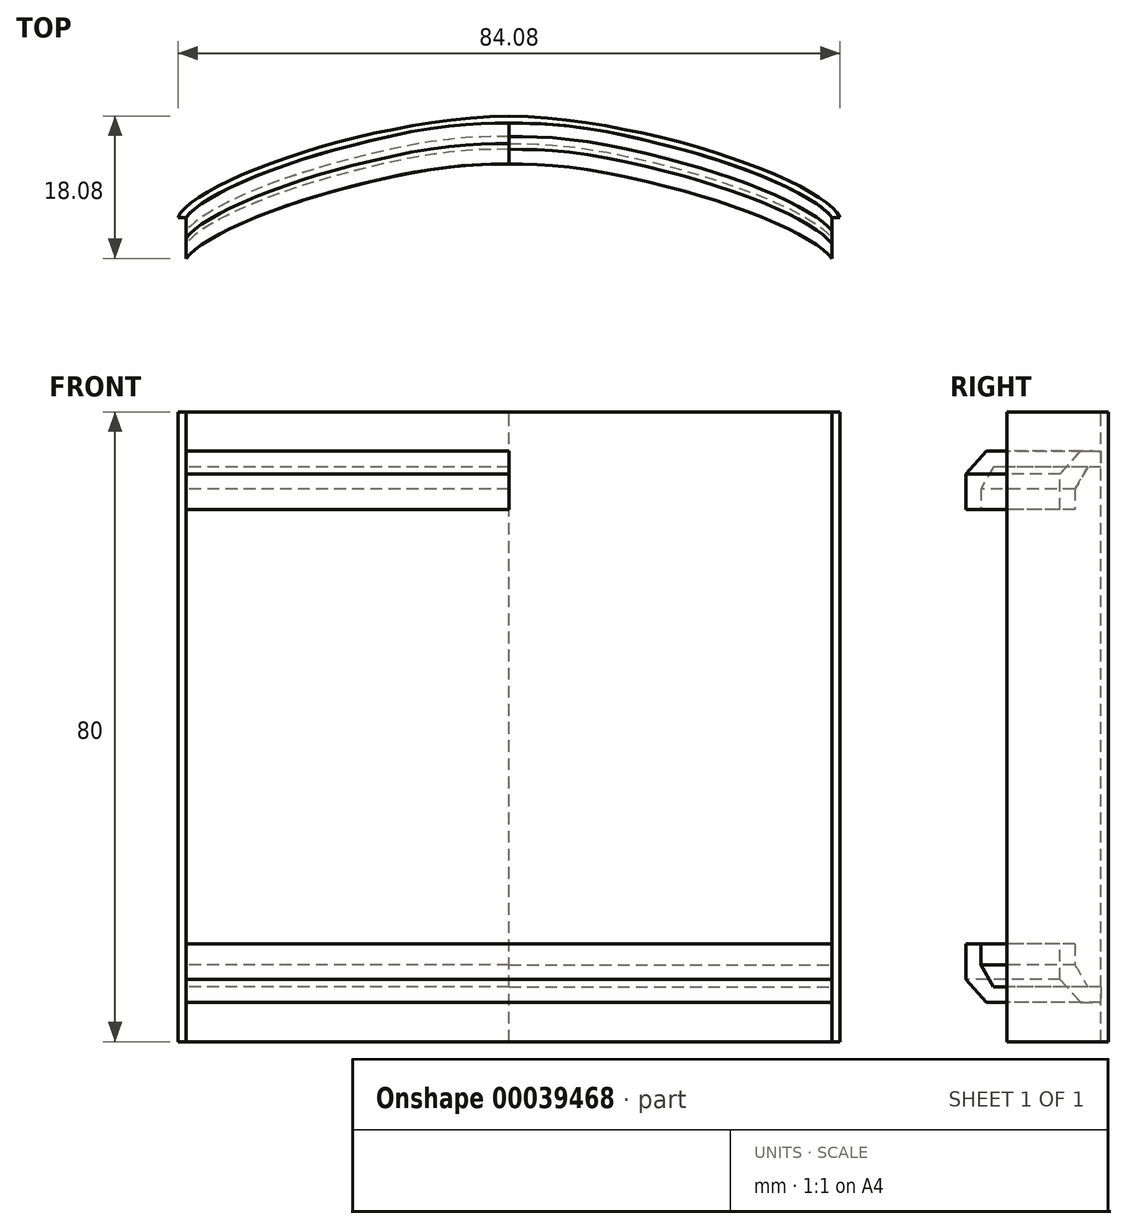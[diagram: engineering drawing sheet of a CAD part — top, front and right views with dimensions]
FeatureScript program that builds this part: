
annotation { "Feature Type Name" : "Feature", "Feature Type Description" : "" }
export const myFeature = defineFeature(function(context is Context, id is Id, definition is map)
    precondition{}
    {
        {
            var Q0;
            Q0=qCreatedBy(makeId("Top.planeOp"),FACE);
            var sketch = newSketch(context, id + "F0", { "sketchPlane" : qUnion([Q0])});
            skFitSpline(sketch, "E0", {"points": [v(-42.04, 0) * mm, v(0, 12.87) * mm], "startDerivative": vector(5.48, 12.98) * mm, "endDerivative": vector(55.38, 1.16) * mm});
            skFitSpline(sketch, "E1.MirrorCS", {"points": [v(42.04, 0) * mm, v(0, 12.87) * mm], "startDerivative": vector(-5.48, 12.98) * mm, "endDerivative": vector(-55.38, 1.16) * mm});
            skFitSpline(sketch, "E2.0", {"points": [v(41.2, -0.35) * mm, v(41.18, -0.28) * mm, v(41.08, -0.1) * mm, v(40.72, 0.36) * mm, v(39.98, 1.06) * mm, v(38.64, 1.99) * mm, v(36.35, 3.31) * mm, v(32.63, 5.04) * mm, v(27.1, 7.09) * mm, v(20.79, 8.95) * mm, v(11.7, 11) * mm, v(4.53, 11.87) * mm, v(-0.02, 11.97) * mm]});
            skFitSpline(sketch, "E2.1", {"points": [v(-41.2, -0.35) * mm, v(-41.18, -0.28) * mm, v(-41.08, -0.1) * mm, v(-40.72, 0.36) * mm, v(-39.98, 1.06) * mm, v(-38.64, 1.99) * mm, v(-36.35, 3.31) * mm, v(-32.63, 5.04) * mm, v(-27.1, 7.09) * mm, v(-20.79, 8.95) * mm, v(-11.7, 11) * mm, v(-4.53, 11.87) * mm, v(0.02, 11.97) * mm]});
            skLineSegment(sketch, "E3", {"start": v(-42.04, 0) * mm, "end": v(-41, 0) * mm});
            skLineSegment(sketch, "E4", {"start": v(41, 0) * mm, "end": v(42.04, 0) * mm});
            skSolve(sketch);
        }
        {
            var Q0;
            Q0=makeQuery(id+"F0.imprint","IMPRINT",FACE,{"disambiguationData":[TD([[makeQuery(id+"F0.imprint","IMPRINT",EDGE,{"derivedFrom":sQuery(id+"F0.wireOp",EDGE,"E0")}),-1.0]])]});
            extrude(context, id + "F1", {"entities" : qUnion([Q0]), "endBound" : BoundingType.SYMMETRIC, "oppositeDirection" : true, "depth" : 80 * mm});
        }
        {
            var Q0;
            Q0=qCreatedBy(makeId("Right.planeOp"),FACE);
            var sketch = newSketch(context, id + "F2", { "sketchPlane" : qUnion([Q0])});
            skLineSegment(sketch, "E5", {"start": v(11.97, 0) * mm, "end": v(11.97, -37.82) * mm, "construction": true});
            skLineSegment(sketch, "E6", {"start": v(11.97, -34.98) * mm, "end": v(11.97, -33.02) * mm});
            skLineSegment(sketch, "E7", {"start": v(11.97, -33.02) * mm, "end": v(10.28, -33.02) * mm});
            skLineSegment(sketch, "E8", {"start": v(10.28, -33.02) * mm, "end": v(8.65, -30.23) * mm});
            skLineSegment(sketch, "E9", {"start": v(8.65, -30.23) * mm, "end": v(8.65, -27.59) * mm});
            skLineSegment(sketch, "E10", {"start": v(8.65, -27.59) * mm, "end": v(6.76, -27.59) * mm});
            skLineSegment(sketch, "E11", {"start": v(6.76, -27.59) * mm, "end": v(6.76, -32.11) * mm});
            skLineSegment(sketch, "E12", {"start": v(6.76, -32.11) * mm, "end": v(9.37, -35.03) * mm});
            skLineSegment(sketch, "E13", {"start": v(9.37, -35.03) * mm, "end": v(11.97, -34.98) * mm});
            skSolve(sketch);
        }
        {
            var Q0;
            Q0=makeQuery(id+"F2.imprint","IMPRINT",FACE,{"disambiguationData":[TD([[makeQuery(id+"F2.imprint","IMPRINT",EDGE,{"derivedFrom":sQuery(id+"F2.wireOp",EDGE,"E6")}),1.0]])]});
            var Q1;
            Q1=makeQuery(id+"F1.opExtrude","CAP_EDGE",EDGE,{"disambiguationData":[OSD([sQuery(id+"F0.wireOp",EDGE,"E2.1")])],"isStart":false});
            sweep(context, id + "F3", {"profiles" : qUnion([Q0]), "path" : qUnion([Q1]), "keepProfileOrientation" : true});
        }
        {
            var Q0;
            Q0=makeQuery(id+"F3.opSweep","CAP_FACE",FACE,{"disambiguationData":[OSD([sQuery(id+"F0.wireOp",EDGE,"E2.0"),sQuery(id+"F0.wireOp",EDGE,"E2.1"),sQuery(id+"F2.wireOp",EDGE,"E6"),sQuery(id+"F2.wireOp",EDGE,"E7"),sQuery(id+"F2.wireOp",EDGE,"E8"),sQuery(id+"F2.wireOp",EDGE,"E9"),sQuery(id+"F2.wireOp",EDGE,"E10"),sQuery(id+"F2.wireOp",EDGE,"E11"),sQuery(id+"F2.wireOp",EDGE,"E12"),sQuery(id+"F2.wireOp",EDGE,"E13")])],"isStart":true});
            var Q1;
            Q1=makeQuery(id+"F1.opExtrude","CAP_EDGE",EDGE,{"disambiguationData":[OSD([sQuery(id+"F0.wireOp",EDGE,"E2.0")])],"isStart":false});
            sweep(context, id + "F4", {"profiles" : qUnion([Q0]), "path" : qUnion([Q1]), "keepProfileOrientation" : true});
        }
        {
            var Q0;
            Q0=makeQuery(id+"F3.opSweep","SWEPT_BODY",BODY,{"disambiguationData":[OSD([sQuery(id+"F0.wireOp",EDGE,"E2.1"),sQuery(id+"F2.wireOp",EDGE,"E6"),sQuery(id+"F2.wireOp",EDGE,"E7"),sQuery(id+"F2.wireOp",EDGE,"E8"),sQuery(id+"F2.wireOp",EDGE,"E9"),sQuery(id+"F2.wireOp",EDGE,"E10"),sQuery(id+"F2.wireOp",EDGE,"E11"),sQuery(id+"F2.wireOp",EDGE,"E12"),sQuery(id+"F2.wireOp",EDGE,"E13")])]});
            var Q1;
            Q1=qCreatedBy(makeId("Top.planeOp"),FACE);
            mirror(context, id + "F5", {"operationType" : NewBodyOperationType.ADD, "entities" : qUnion([Q0]), "mirrorPlane" : qUnion([Q1])});
        }
    });
